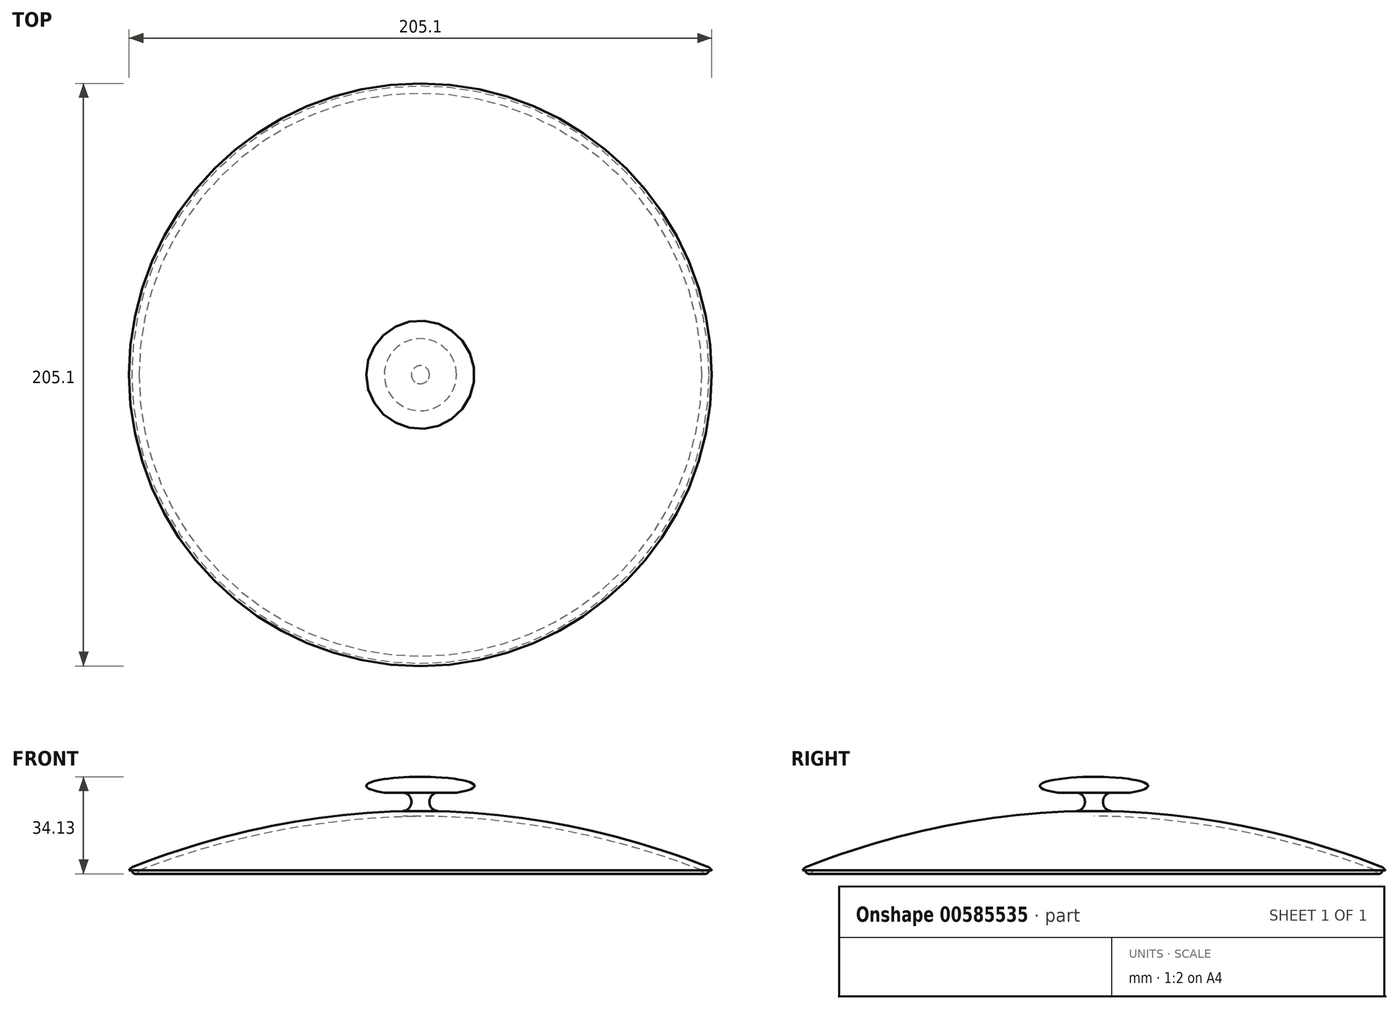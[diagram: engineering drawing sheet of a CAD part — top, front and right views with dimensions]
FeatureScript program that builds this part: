
annotation { "Feature Type Name" : "Feature", "Feature Type Description" : "" }
export const myFeature = defineFeature(function(context is Context, id is Id, definition is map)
    precondition{}
    {
        {
            var Q0;
            Q0=qCreatedBy(makeId("Front.planeOp"),FACE);
            var sketch = newSketch(context, id + "F0", { "sketchPlane" : qUnion([Q0])});
            skArc(sketch, "E0", {"start": v(0, 19.05) * mm, "mid": v(-50.38, 13.97) * mm, "end": v(-99.06, 0) * mm});
            skArc(sketch, "E1.0", {"start": v(0, 20.95) * mm, "mid": v(-52.21, 15.55) * mm, "end": v(-102.55, 0.67) * mm});
            skLineSegment(sketch, "E2", {"start": v(-99.06, 0) * mm, "end": v(-102.55, 0) * mm});
            skPoint(sketch, "E3", {"position": v(-101.6, 0) * mm});
            skArc(sketch, "E4", {"start": v(-101.6, 0) * mm, "mid": v(-100.33, -1.27) * mm, "end": v(-99.06, 0) * mm});
            skLineSegment(sketch, "E5", {"start": v(0, 20.95) * mm, "end": v(0, 19.05) * mm});
            skLineSegment(sketch, "E6", {"start": v(0, 11.03) * mm, "end": v(0, 22.85) * mm});
            skLineSegment(sketch, "E7", {"start": v(34.16, 0) * mm, "end": v(-309.5, 0) * mm, "construction": true});
            skPoint(sketch, "E8", {"position": v(-50.38, 13.97) * mm});
            skEllipticalArc(sketch, "E9", {});
            skLineSegment(sketch, "E10", {"start": v(-12.7, 27.31) * mm, "end": v(0, 27.31) * mm});
            skLineSegment(sketch, "E11", {"start": v(0, 20.95) * mm, "end": v(0, 32.86) * mm});
            skLineSegment(sketch, "E12", {"start": v(-3.17, 27.31) * mm, "end": v(-3.17, 20.9) * mm});
            skPoint(sketch, "E13.start.orphan", {"position": v(-284.18, -48.49) * mm});
            skPoint(sketch, "E14.end.orphan", {"position": v(-488.4, -48.49) * mm});
            skLineSegment(sketch, "E15", {"start": v(-102.55, 0) * mm, "end": v(-102.55, 0.67) * mm});
            skPoint(sketch, "E16", {"position": v(-19.05, 29.68) * mm});
            const initialGuessF0  = {"E9": [0, 0.029680962849168272, -1, 0, 0.01905, 0.003175, 4.71238898038469, 0.841068670568102]};
            skSetInitialGuess(sketch, initialGuessF0);
            skSolve(sketch);
        }
        {
            var Q0;
            Q0 = qSketchRegion(id + "F0", true);
            var Q1;
            Q1=sQuery(id+"F0.wireOp",EDGE,"E6");
            revolve(context, id + "F1", {"entities" : qUnion([Q0]), "axis" : qUnion([Q1]), "revolveType" : RevolveType.FULL});
        }
        {
            var Q0;
            Q0=makeQuery(id+"F1.opRevolve","SWEPT_EDGE",EDGE,{"disambiguationData":[OSD([sQuery(id+"F0.wireOp",EDGE,"E1.0"),sQuery(id+"F0.wireOp",EDGE,"E15")])]});
            fillet(context, id + "F2", {"entities" : qUnion([Q0]), "radius" : 3.17 * mm, "tangentPropagation" : true, "allowEdgeOverflow" : false});
        }
        {
            var Q0;
            Q0=makeQuery(id+"F1.opRevolve","SWEPT_EDGE",EDGE,{"disambiguationData":[OSD([sQuery(id+"F0.wireOp",EDGE,"E1.0"),sQuery(id+"F0.wireOp",EDGE,"E12")])]});
            var Q1;
            Q1=makeQuery(id+"F1.opRevolve","SWEPT_EDGE",EDGE,{"disambiguationData":[OSD([sQuery(id+"F0.wireOp",EDGE,"E10"),sQuery(id+"F0.wireOp",EDGE,"E12")])]});
            fillet(context, id + "F3", {"entities" : qUnion([Q0, Q1]), "radius" : 3.17 * mm, "tangentPropagation" : true, "allowEdgeOverflow" : false});
        }
    });
